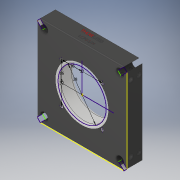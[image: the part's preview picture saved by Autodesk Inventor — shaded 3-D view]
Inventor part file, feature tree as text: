
AUTODESK INVENTOR PART (.ipt)
format: ipt  version: 2017 (Build 210142000, 142)  size: 902,144 bytes
history: native  units: mm
features: extrude x2, sketch x1, hole x1, fillet x1, other x1
ambient origin geometry x8: Origin, YZ Plane, XZ Plane, XY Plane, X Axis, Y Axis, Z Axis, Center Point
bodies: Solid1 (feature_tree)
feature tree (6):
  sketch  "Sketch4"  dims[d40=38.0mm d41=16.0mm d42=16.0mm d43=20.0mm d45=32.0mm d46=20.0mm d48=32.0mm d51=2.5mm d52=6.0mm d53=4.0mm d54=2.0mm d55=90.0deg d56=8.0mm d57=20.594885mm d58=10.0mm d59=0.0mm d60=2.0mm d61=10.0mm d62=0.0mm]
  hole  "Hole5"  [1 undecoded]
  extrude  "Extrusion3"  Depth=16.0mm
  fillet  "Fillet1"  Radius=20.0mm
  extrude  "Extrusion4"  Depth=10.0mm TaperAngle=0.0deg
  other  "13108-001-1-solid1"
note: 1 required parameter value undecoded (feature->parameter linkage not recoverable at this tier; creation-order binding heuristic only, values carry confidence <= 0.55)
